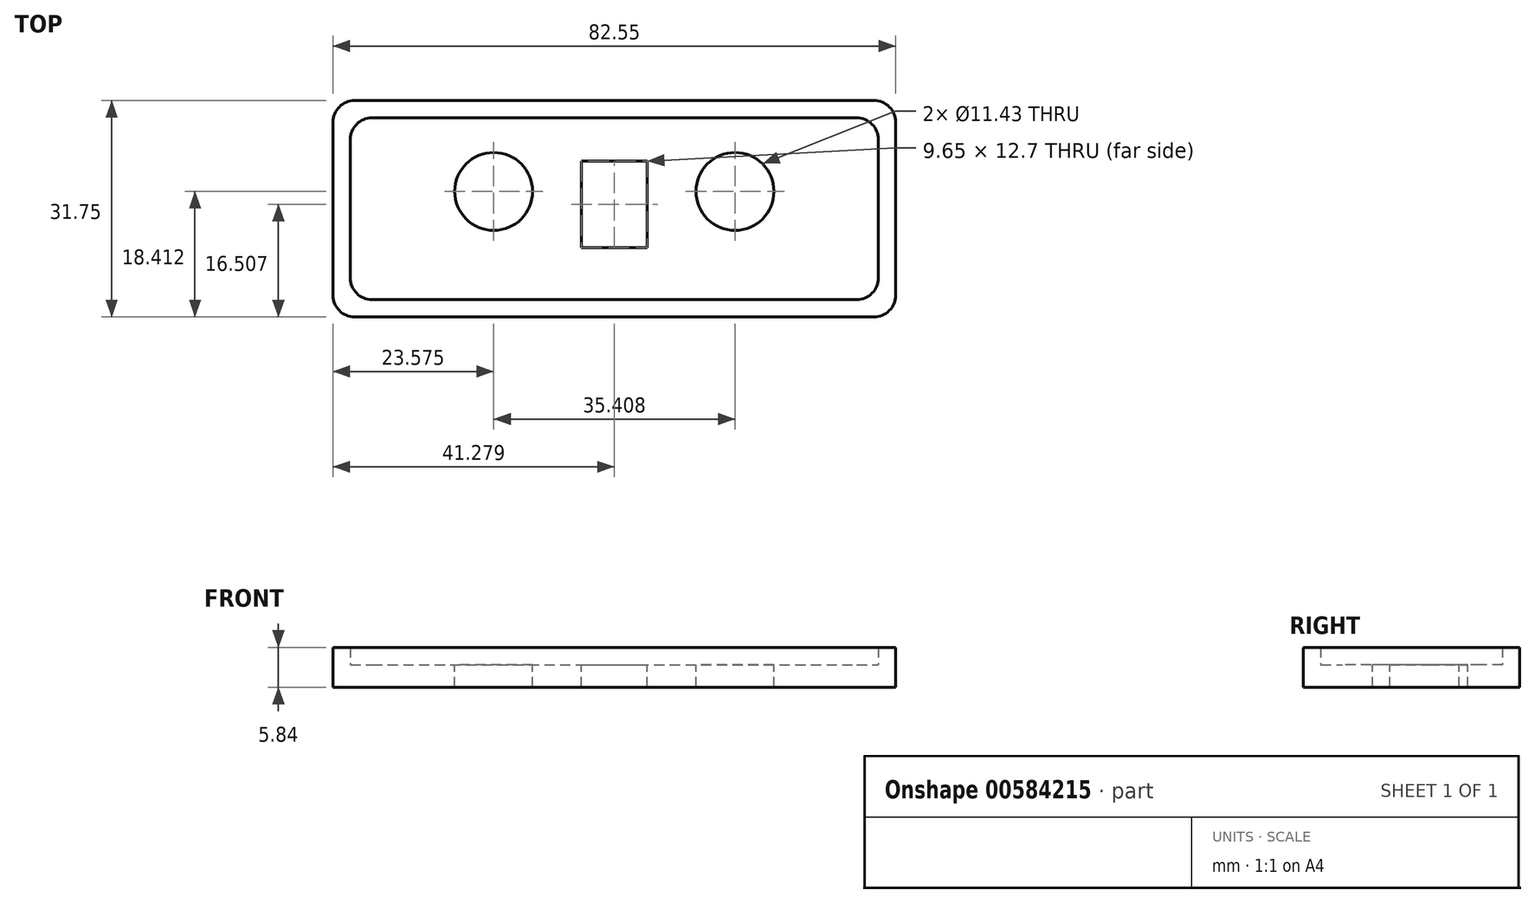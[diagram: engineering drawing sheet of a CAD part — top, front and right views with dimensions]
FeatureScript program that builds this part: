
annotation { "Feature Type Name" : "Feature", "Feature Type Description" : "" }
export const myFeature = defineFeature(function(context is Context, id is Id, definition is map)
    precondition{}
    {
        {
            var Q0;
            Q0=qCreatedBy(makeId("Top.planeOp"),FACE);
            var sketch = newSketch(context, id + "F0", { "sketchPlane" : qUnion([Q0])});
            skLineSegment(sketch, "E0.bottom", {"start": v(12.86, -33.07) * mm, "end": v(83.98, -33.07) * mm});
            skLineSegment(sketch, "E0.top", {"start": v(12.86, -6.4) * mm, "end": v(83.98, -6.4) * mm});
            skLineSegment(sketch, "E0.left", {"start": v(9.68, -9.58) * mm, "end": v(9.68, -29.9) * mm});
            skLineSegment(sketch, "E0.right", {"start": v(87.15, -9.58) * mm, "end": v(87.15, -29.9) * mm});
            skPoint(sketch, "E1", {"position": v(48.42, -6.4) * mm});
            skPoint(sketch, "E2", {"position": v(9.68, -19.74) * mm});
            skLineSegment(sketch, "E3.0", {"start": v(10.32, -3.86) * mm, "end": v(86.52, -3.86) * mm});
            skLineSegment(sketch, "E3.1", {"start": v(7.14, -7.04) * mm, "end": v(7.14, -32.44) * mm});
            skLineSegment(sketch, "E3.2", {"start": v(10.32, -35.61) * mm, "end": v(86.52, -35.61) * mm});
            skLineSegment(sketch, "E3.3", {"start": v(89.7, -7.04) * mm, "end": v(89.7, -32.44) * mm});
            skPoint(sketch, "E4.visualSharp", {"position": v(87.15, -33.07) * mm});
            skArc(sketch, "E4.filletArc", {"start": v(83.98, -33.07) * mm, "mid": v(86.22, -32.14) * mm, "end": v(87.15, -29.9) * mm});
            skPoint(sketch, "E5.visualSharp", {"position": v(87.15, -6.4) * mm});
            skArc(sketch, "E5.filletArc", {"start": v(87.15, -9.58) * mm, "mid": v(86.22, -7.33) * mm, "end": v(83.98, -6.4) * mm});
            skPoint(sketch, "E6.visualSharp", {"position": v(89.7, -35.61) * mm});
            skArc(sketch, "E6.filletArc", {"start": v(86.52, -35.61) * mm, "mid": v(88.76, -34.68) * mm, "end": v(89.7, -32.44) * mm});
            skPoint(sketch, "E7.visualSharp", {"position": v(89.7, -3.86) * mm});
            skArc(sketch, "E7.filletArc", {"start": v(89.7, -7.04) * mm, "mid": v(88.76, -4.8) * mm, "end": v(86.52, -3.86) * mm});
            skPoint(sketch, "E8.visualSharp", {"position": v(9.68, -33.07) * mm});
            skArc(sketch, "E8.filletArc", {"start": v(9.68, -29.9) * mm, "mid": v(10.61, -32.14) * mm, "end": v(12.86, -33.07) * mm});
            skPoint(sketch, "E9.visualSharp", {"position": v(7.14, -35.61) * mm});
            skArc(sketch, "E9.filletArc", {"start": v(7.14, -32.44) * mm, "mid": v(8.07, -34.68) * mm, "end": v(10.32, -35.61) * mm});
            skPoint(sketch, "E10.visualSharp", {"position": v(7.14, -3.86) * mm});
            skArc(sketch, "E10.filletArc", {"start": v(10.32, -3.86) * mm, "mid": v(8.07, -4.8) * mm, "end": v(7.14, -7.04) * mm});
            skPoint(sketch, "E11.visualSharp", {"position": v(9.68, -6.4) * mm});
            skArc(sketch, "E11.filletArc", {"start": v(12.86, -6.4) * mm, "mid": v(10.61, -7.33) * mm, "end": v(9.68, -9.58) * mm});
            skSolve(sketch);
        }
        {
            var Q0;
            Q0=makeQuery(id+"F0.imprint","IMPRINT",FACE,{"disambiguationData":[TD([[makeQuery(id+"F0.imprint","IMPRINT",EDGE,{"derivedFrom":sQuery(id+"F0.wireOp",EDGE,"E0.bottom")}),-1.0]])]});
            var Q1;
            Q1=makeQuery(id+"F0.imprint","IMPRINT",FACE,{"disambiguationData":[TD([[makeQuery(id+"F0.imprint","IMPRINT",EDGE,{"derivedFrom":sQuery(id+"F0.wireOp",EDGE,"E0.bottom")}),1.0]])]});
            extrude(context, id + "F1", {"entities" : qUnion([Q0, Q1]), "oppositeDirection" : true, "depth" : 3.3 * mm, "offsetDistance" : 25.4 * mm});
        }
        {
            var Q0;
            Q0=makeQuery(id+"F0.imprint","IMPRINT",FACE,{"disambiguationData":[TD([[makeQuery(id+"F0.imprint","IMPRINT",EDGE,{"derivedFrom":sQuery(id+"F0.wireOp",EDGE,"E0.bottom")}),-1.0]])]});
            extrude(context, id + "F2", {"entities" : qUnion([Q0]), "operationType" : NewBodyOperationType.ADD, "depth" : 2.54 * mm, "offsetDistance" : 25.4 * mm});
        }
        {
            var Q0;
            Q0=qCreatedBy(makeId("Top.planeOp"),FACE);
            var sketch = newSketch(context, id + "F3", { "sketchPlane" : qUnion([Q0])});
            skCircle(sketch, "E12", {"center": v(30.72, -17.2) * mm, "radius": 5.72 * mm});
            skCircle(sketch, "E13", {"center": v(66.12, -17.2) * mm, "radius": 5.72 * mm});
            skLineSegment(sketch, "E14.bottom", {"start": v(43.6, -12.75) * mm, "end": v(53.24, -12.75) * mm});
            skLineSegment(sketch, "E14.top", {"start": v(43.6, -25.45) * mm, "end": v(53.24, -25.45) * mm});
            skLineSegment(sketch, "E14.left", {"start": v(43.6, -12.75) * mm, "end": v(43.6, -25.45) * mm});
            skLineSegment(sketch, "E14.right", {"start": v(53.24, -12.75) * mm, "end": v(53.24, -25.45) * mm});
            skPoint(sketch, "E15", {"position": v(48.42, -12.75) * mm});
            skLineSegment(sketch, "E16", {"start": v(30.72, -17.2) * mm, "end": v(66.12, -17.2) * mm});
            skPoint(sketch, "E17", {"position": v(48.42, -17.2) * mm});
            skSolve(sketch);
        }
        {
            var Q0;
            Q0 = qSketchRegion(id + "F3", true);
            extrude(context, id + "F4", {"entities" : qUnion([Q0]), "operationType" : NewBodyOperationType.REMOVE, "endBound" : BoundingType.THROUGH_ALL, "oppositeDirection" : true, "depth" : 25.4 * mm, "offsetDistance" : 25.4 * mm});
        }
    });
